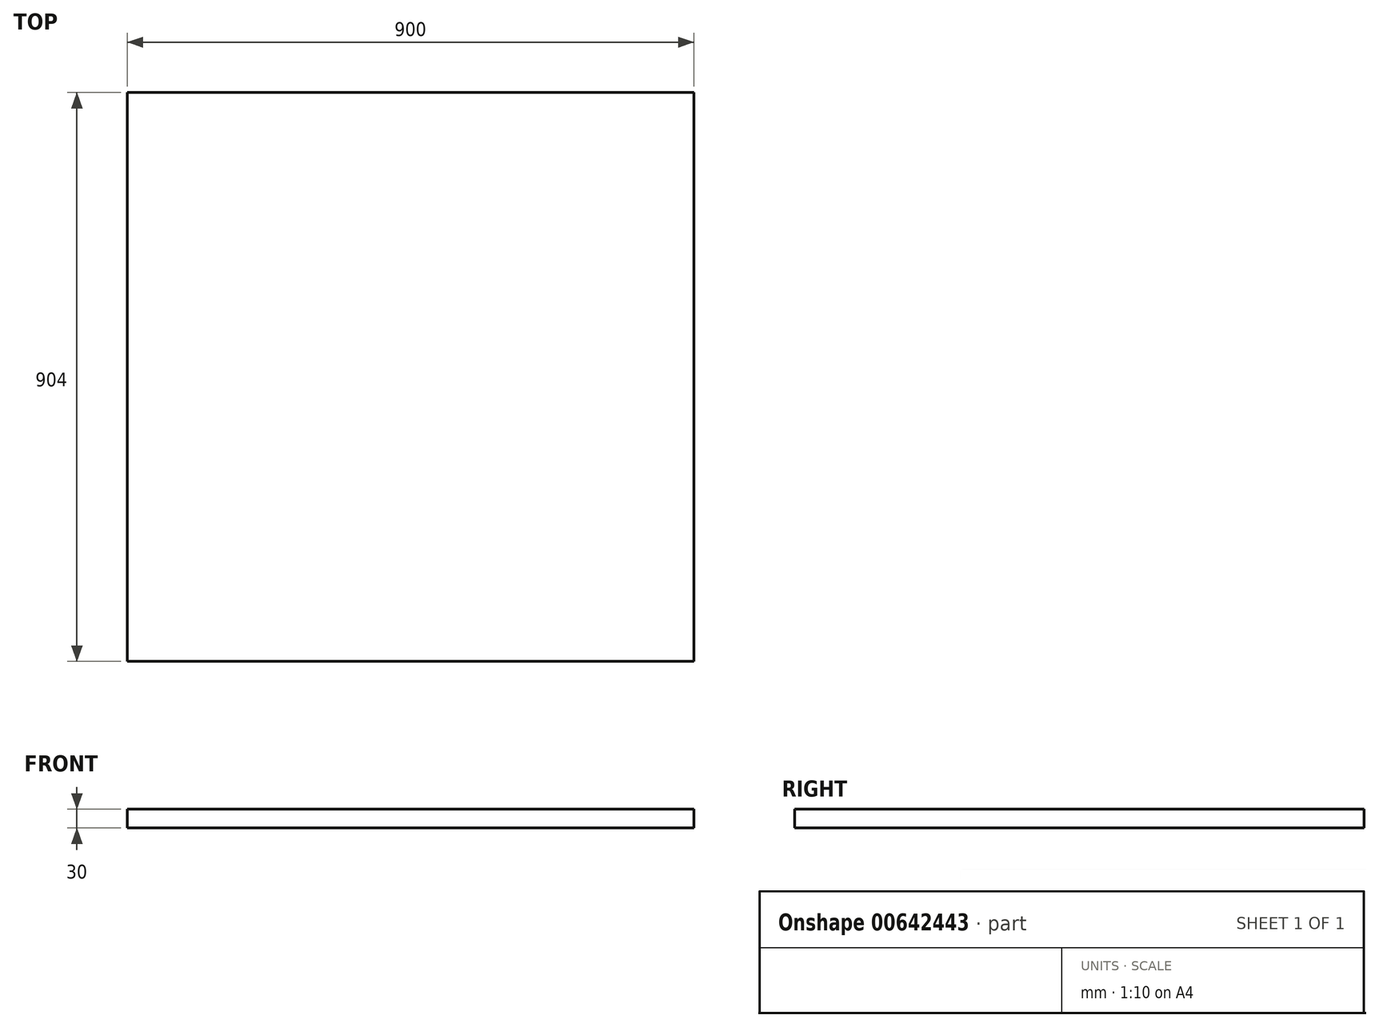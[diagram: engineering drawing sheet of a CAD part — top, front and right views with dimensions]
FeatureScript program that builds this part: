
annotation { "Feature Type Name" : "Feature", "Feature Type Description" : "" }
export const myFeature = defineFeature(function(context is Context, id is Id, definition is map)
    precondition{}
    {
        {
            var Q0;
            Q0=qCreatedBy(makeId("Top.planeOp"),FACE);
            var sketch = newSketch(context, id + "F0", { "sketchPlane" : qUnion([Q0])});
            skLineSegment(sketch, "E0.bottom", {"start": v(322.26, 327) * mm, "end": v(-327.74, 327) * mm});
            skLineSegment(sketch, "E0.top", {"start": v(322.26, -327) * mm, "end": v(-327.74, -327) * mm});
            skLineSegment(sketch, "E0.left", {"start": v(322.26, 327) * mm, "end": v(322.26, -327) * mm});
            skLineSegment(sketch, "E0.right", {"start": v(-327.74, 327) * mm, "end": v(-327.74, -327) * mm});
            skPoint(sketch, "E0.middle", {"position": v(-2.74, 0) * mm});
            skSolve(sketch);
        }
        {
            var Q0;
            Q0 = qSketchRegion(id + "F0", true);
            extrude(context, id + "F1", {"entities" : qUnion([Q0]), "depth" : 30 * mm, "offsetDistance" : 25 * mm});
        }
        {
            var Q0;
            Q0=makeQuery(id+"F1.opExtrude","SWEPT_FACE",FACE,{"disambiguationData":[OSD([sQuery(id+"F0.wireOp",EDGE,"E0.top")])]});
            extrude(context, id + "F2", {"entities" : qUnion([Q0]), "operationType" : NewBodyOperationType.ADD, "depth" : 250 * mm, "offsetDistance" : 25 * mm});
        }
        {
            var Q0;
            {var subQ0=sQuery(id+"F0.wireOp",EDGE,"E0.left");Q0=makeQuery(id+"F2.boolean.opBoolean","MERGE",FACE,{"derivedFrom":[makeQuery(id+"F1.opExtrude","SWEPT_FACE",FACE,{"disambiguationData":[OSD([subQ0])]}),makeQuery(id+"F2.opExtrude","SWEPT_FACE",FACE,{"disambiguationData":[OSD([sQuery(id+"F0.wireOp",EDGE,"E0.top"),subQ0])]})]});}
            extrude(context, id + "F3", {"entities" : qUnion([Q0]), "operationType" : NewBodyOperationType.ADD, "depth" : 250 * mm, "offsetDistance" : 25 * mm});
        }
    });
